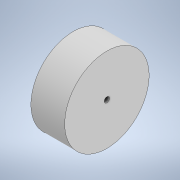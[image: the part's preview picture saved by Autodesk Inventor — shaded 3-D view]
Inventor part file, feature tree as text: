
AUTODESK INVENTOR PART (.ipt)
format: ipt  version: 2020.1 (Build 241239000, 239)  size: 94,208 bytes
history: native  units: mm
features: extrude x1, sketch x1
ambient origin geometry x8: Origin, YZ Plane, XZ Plane, XY Plane, X Axis, Y Axis, Z Axis, Center Point
bodies: Solid1 (feature_tree)
feature tree (2):
  extrude  "Extrusion1"  Depth=20.32mm
  sketch  "Sketch1"  dims[d0=50.8mm d1=3.175mm d2=20.32mm d3=0.0mm]
